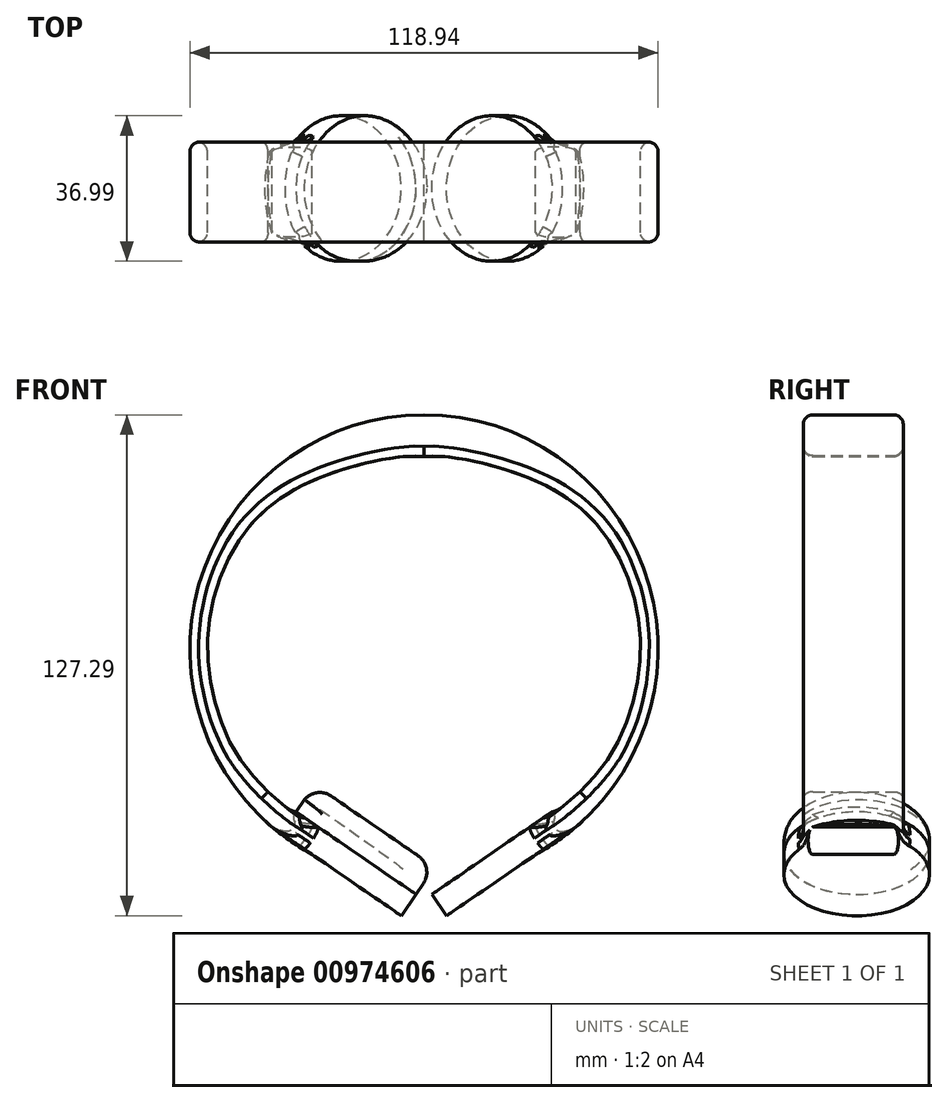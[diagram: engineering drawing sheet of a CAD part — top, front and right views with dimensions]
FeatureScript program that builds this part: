
annotation { "Feature Type Name" : "Feature", "Feature Type Description" : "" }
export const myFeature = defineFeature(function(context is Context, id is Id, definition is map)
    precondition{}
    {
        {
            var Q0;
            Q0=qCreatedBy(makeId("Right.planeOp"),FACE);
            cPlane(context, id + "F0", {"entities" : qUnion([Q0]), "cplaneType" : CPlaneType.OFFSET, "offset" : 59.69 * mm, "oppositeDirection" : true, "width" : 152.4 * mm, "height" : 152.4 * mm});
        }
        {
            var Q0;
            Q0=qCreatedBy(makeId("Front.planeOp"),FACE);
            var sketch = newSketch(context, id + "F1", { "sketchPlane" : qUnion([Q0])});
            skCircle(sketch, "E0", {"center": v(0, 0) * mm, "radius": 59.47 * mm});
            skFitSpline(sketch, "E1", {"points": [v(-39.6, -36.29) * mm, v(-49.04, -24.15) * mm, v(-55.01, 0) * mm, v(-49.81, 22.66) * mm, v(-35.56, 38.85) * mm, v(-9.35, 48.29) * mm, v(0, 48.86) * mm, v(0, 48.67) * mm], "startDerivative": vector(-69.88, 72.92) * mm, "endDerivative": vector(-4.83, -12.64) * mm});
            skLineSegment(sketch, "E2", {"start": v(0, 67.87) * mm, "end": v(0, -66.03) * mm});
            skLineSegment(sketch, "E3", {"start": v(0.03, 48.74) * mm, "end": v(0.03, 59.47) * mm});
            skFitSpline(sketch, "E4.MirrorCS", {"points": [v(39.6, -36.29) * mm, v(49.04, -24.15) * mm, v(55.01, 0) * mm, v(49.81, 22.66) * mm, v(35.56, 38.85) * mm, v(9.35, 48.29) * mm, v(0, 48.86) * mm, v(0, 48.67) * mm], "startDerivative": vector(69.88, 72.92) * mm, "endDerivative": vector(4.83, -12.64) * mm});
            skLineSegment(sketch, "E5.MirrorCS", {"start": v(39.6, -36.29) * mm, "end": v(42.95, -41.13) * mm});
            skPoint(sketch, "E6", {"position": v(-11.33, -63.99) * mm});
            skFitSpline(sketch, "E7", {"points": [v(-39.6, -36.29) * mm, v(-32.33, -42.32) * mm, v(-26.08, -45.97) * mm], "startDerivative": vector(13.7, -12.25) * mm, "endDerivative": vector(13.34, -7) * mm});
            skLineSegment(sketch, "E8", {"start": v(-26.08, -45.97) * mm, "end": v(-28.38, -52.26) * mm});
            skSolve(sketch);
        }
        {
            var Q0;
            {var subQ0=sQuery(id+"F1.wireOp",EDGE,"yAXJTIKi-DCpe-Cwv5-86Dl-3V6B5zLxSxU3");Q0=makeQuery(id+"F1.imprint","IMPRINT",FACE,{"disambiguationData":[TD([[makeQuery(id+"F1.imprint","IMPRINT",EDGE,{"derivedFrom":subQ0}),-1.0]])]});}
            var Q1;
            {var subQ0=sQuery(id+"F1.wireOp",EDGE,"E7");Q1=makeQuery(id+"F1.imprint","IMPRINT",FACE,{"disambiguationData":[TD([[makeQuery(id+"F1.imprint","IMPRINT",EDGE,{"derivedFrom":subQ0}),-1.0]])]});}
            extrude(context, id + "F2", {"entities" : qUnion([Q0, Q1]), "depth" : 25.4 * mm, "offsetDistance" : 25.4 * mm});
        }
        {
            var Q0;
            Q0=makeQuery(id+"F2.opExtrude","CAP_EDGE",EDGE,{"disambiguationData":[OSD([sQuery(id+"F1.wireOp",EDGE,"E1")])],"isStart":false});
            var Q1;
            {var subQ0=sQuery(id+"F1.wireOp",EDGE,"E0");Q1=makeQuery(id+"F2.opExtrude","CAP_EDGE",EDGE,{"disambiguationData":[OSD([subQ0]),TDD([makeQuery(id+"F1.imprint","IMPRINT",EDGE,{"disambiguationData":[TD([[makeQuery(id+"F1.imprint","INTERSECT",VERTEX,{"derivedFrom":[subQ0,sQuery(id+"F1.wireOp",EDGE,"yAXJTIKi-DCpe-Cwv5-86Dl-3V6B5zLxSxU3")]}),1.0]])],"derivedFrom":subQ0})])],"isStart":false});}
            var Q2;
            Q2=makeQuery(id+"F2.opExtrude","CAP_EDGE",EDGE,{"disambiguationData":[OSD([sQuery(id+"F1.wireOp",EDGE,"E0")])],"isStart":true});
            var Q3;
            Q3=makeQuery(id+"F2.opExtrude","CAP_EDGE",EDGE,{"disambiguationData":[OSD([sQuery(id+"F1.wireOp",EDGE,"E1")])],"isStart":true});
            var Q4;
            Q4=makeQuery(id+"F2.opExtrude","CAP_EDGE",EDGE,{"disambiguationData":[OSD([sQuery(id+"F1.wireOp",EDGE,"E7")])],"isStart":false});
            var Q5;
            Q5=makeQuery(id+"F2.opExtrude","CAP_EDGE",EDGE,{"disambiguationData":[OSD([sQuery(id+"F1.wireOp",EDGE,"E7")])],"isStart":true});
            fillet(context, id + "F3", {"entities" : qUnion([Q0, Q1, Q2, Q3, Q4, Q5]), "radius" : 2.45 * mm, "tangentPropagation" : true, "allowEdgeOverflow" : false});
        }
        {
            var Q0;
            Q0=sQuery(id+"F1.wireOp",VERTEX,"E6");
            var Q1;
            {var subQ0=sQuery(id+"F1.wireOp",EDGE,"E0");Q1=makeQuery(id+"F3.opFillet","BLEND_VERTEX",VERTEX,{"blendedFrom":[makeQuery(id+"F2.opExtrude","CAP_EDGE",EDGE,{"disambiguationData":[OSD([subQ0])],"isStart":false}),makeQuery(id+"F2.opExtrude","SWEPT_FACE",FACE,{"disambiguationData":[OSD([subQ0])]}),makeQuery(id+"F2.opExtrude","SWEPT_FACE",FACE,{"disambiguationData":[OSD([sQuery(id+"F1.wireOp",EDGE,"E8")])]})],"blendedInto":[makeQuery(id+"F2.opExtrude","SWEPT_FACE",FACE,{"disambiguationData":[OSD([subQ0])]}),makeQuery(id+"F2.opExtrude","SWEPT_FACE",FACE,{"disambiguationData":[OSD([sQuery(id+"F1.wireOp",EDGE,"E8")])]})]});}
            var Q2;
            {var subQ0=sQuery(id+"F1.wireOp",EDGE,"E0");Q2=makeQuery(id+"F3.opFillet","BLEND_VERTEX",VERTEX,{"blendedFrom":[makeQuery(id+"F2.opExtrude","CAP_EDGE",EDGE,{"disambiguationData":[OSD([subQ0])],"isStart":true}),makeQuery(id+"F2.opExtrude","SWEPT_FACE",FACE,{"disambiguationData":[OSD([subQ0])]}),makeQuery(id+"F2.opExtrude","SWEPT_FACE",FACE,{"disambiguationData":[OSD([sQuery(id+"F1.wireOp",EDGE,"E8")])]})],"blendedInto":[makeQuery(id+"F2.opExtrude","SWEPT_FACE",FACE,{"disambiguationData":[OSD([subQ0])]}),makeQuery(id+"F2.opExtrude","SWEPT_FACE",FACE,{"disambiguationData":[OSD([sQuery(id+"F1.wireOp",EDGE,"E8")])]})]});}
            cPlane(context, id + "F4", {"entities" : qUnion([Q0, Q1, Q2]), "cplaneType" : CPlaneType.THREE_POINT, "offset" : 25.4 * mm, "width" : 152.4 * mm, "height" : 152.4 * mm});
        }
        {
            var Q0;
            Q0=qCreatedBy(id+"F4.planeOp",FACE);
            var sketch = newSketch(context, id + "F5", { "sketchPlane" : qUnion([Q0])});
            skCircle(sketch, "E9", {"center": v(15.19, -11.8) * mm, "radius": 18.5 * mm});
            skSolve(sketch);
        }
        {
            var Q0;
            Q0=qSketchRegion(id+"F5",true);
            extrude(context, id + "F6", {"entities" : qUnion([Q0]), "operationType" : NewBodyOperationType.ADD, "depth" : 6.6 * mm, "offsetDistance" : 25.4 * mm});
        }
        {
            var Q0;
            {var subQ0=sQuery(id+"F1.wireOp",EDGE,"E0");Q0=makeQuery(id+"F6.boolean.opBoolean","INTERSECT",EDGE,{"derivedFrom":[makeQuery(id+"F3.opFillet","BLEND_FACE",FACE,{"disambiguationData":[OSD([subQ0]),TDD([makeQuery(id+"F2.opExtrude","CAP_EDGE",EDGE,{"disambiguationData":[OSD([subQ0])],"isStart":true})])]}),makeQuery(id+"F6.opExtrude","SWEPT_FACE",FACE,{"disambiguationData":[OSD([sQuery(id+"F5.wireOp",EDGE,"E9")])]})]});}
            fillet(context, id + "F7", {"entities" : qUnion([Q0]), "radius" : 6.27 * mm, "tangentPropagation" : true, "allowEdgeOverflow" : false});
        }
        {
            var Q0;
            Q0=makeQuery(id+"F6.opExtrude","CAP_FACE",FACE,{"disambiguationData":[OSD([sQuery(id+"F5.wireOp",EDGE,"E9")])],"isStart":false});
            var sketch = newSketch(context, id + "F8", { "sketchPlane" : qUnion([Q0])});
            skCircle(sketch, "E10", {"center": v(15.16, -11.78) * mm, "radius": 18.5 * mm});
            skSolve(sketch);
        }
        {
            var Q0;
            Q0=makeQuery(id+"F2.opExtrude","SWEPT_BODY",BODY,{"disambiguationData":[OSD([sQuery(id+"F1.wireOp",EDGE,"E0"),sQuery(id+"F1.wireOp",EDGE,"E1"),sQuery(id+"F1.wireOp",EDGE,"E2"),sQuery(id+"F1.wireOp",EDGE,"E7"),sQuery(id+"F1.wireOp",EDGE,"E8")])]});
            var Q1;
            Q1=qCreatedBy(makeId("Right.planeOp"),FACE);
            mirror(context, id + "F9", {"operationType" : NewBodyOperationType.ADD, "entities" : qUnion([Q0]), "mirrorPlane" : qUnion([Q1])});
        }
        {
            var Q0;
            {var subQ0=sQuery(id+"F5.wireOp",EDGE,"E9");var subQ1=makeQuery(id+"F6.opExtrude","CAP_FACE",FACE,{"disambiguationData":[OSD([subQ0])],"isStart":false});var subQ2=makeQuery(id+"F6.opExtrude","SWEPT_FACE",FACE,{"disambiguationData":[OSD([subQ0])]});var subQ3=sQuery(id+"F1.wireOp",EDGE,"E7");var subQ4=makeQuery(id+"F7.opFillet","BLEND_EDGE",EDGE,{"blendedFrom":[makeQuery(id+"F6.boolean.opBoolean","INTERSECT",EDGE,{"derivedFrom":[makeQuery(id+"F3.opFillet","BLEND_FACE",FACE,{"disambiguationData":[OSD([subQ3]),TDD([makeQuery(id+"F2.opExtrude","CAP_EDGE",EDGE,{"disambiguationData":[OSD([subQ3])],"isStart":true})])]}),subQ2]}),subQ1],"blendedInto":[subQ1]});Q0=makeQuery(id+"F8.imprint","IMPRINT",FACE,{"disambiguationData":[TD([[makeQuery(id+"F8.imprint","IMPRINT",EDGE,{"derivedFrom":subQ4}),1.0]])]});}
            extrude(context, id + "F10", {"entities" : qUnion([Q0]), "operationType" : NewBodyOperationType.ADD, "depth" : 8.38 * mm, "offsetDistance" : 25.4 * mm});
        }
        {
            var Q0;
            Q0=makeQuery(id+"F10.opExtrude","CAP_EDGE",EDGE,{"disambiguationData":[OSD([sQuery(id+"F8.wireOp",EDGE,"E10")])],"isStart":false});
            fillet(context, id + "F11", {"entities" : qUnion([Q0]), "radius" : 5.08 * mm, "tangentPropagation" : true, "allowEdgeOverflow" : false});
        }
    });
